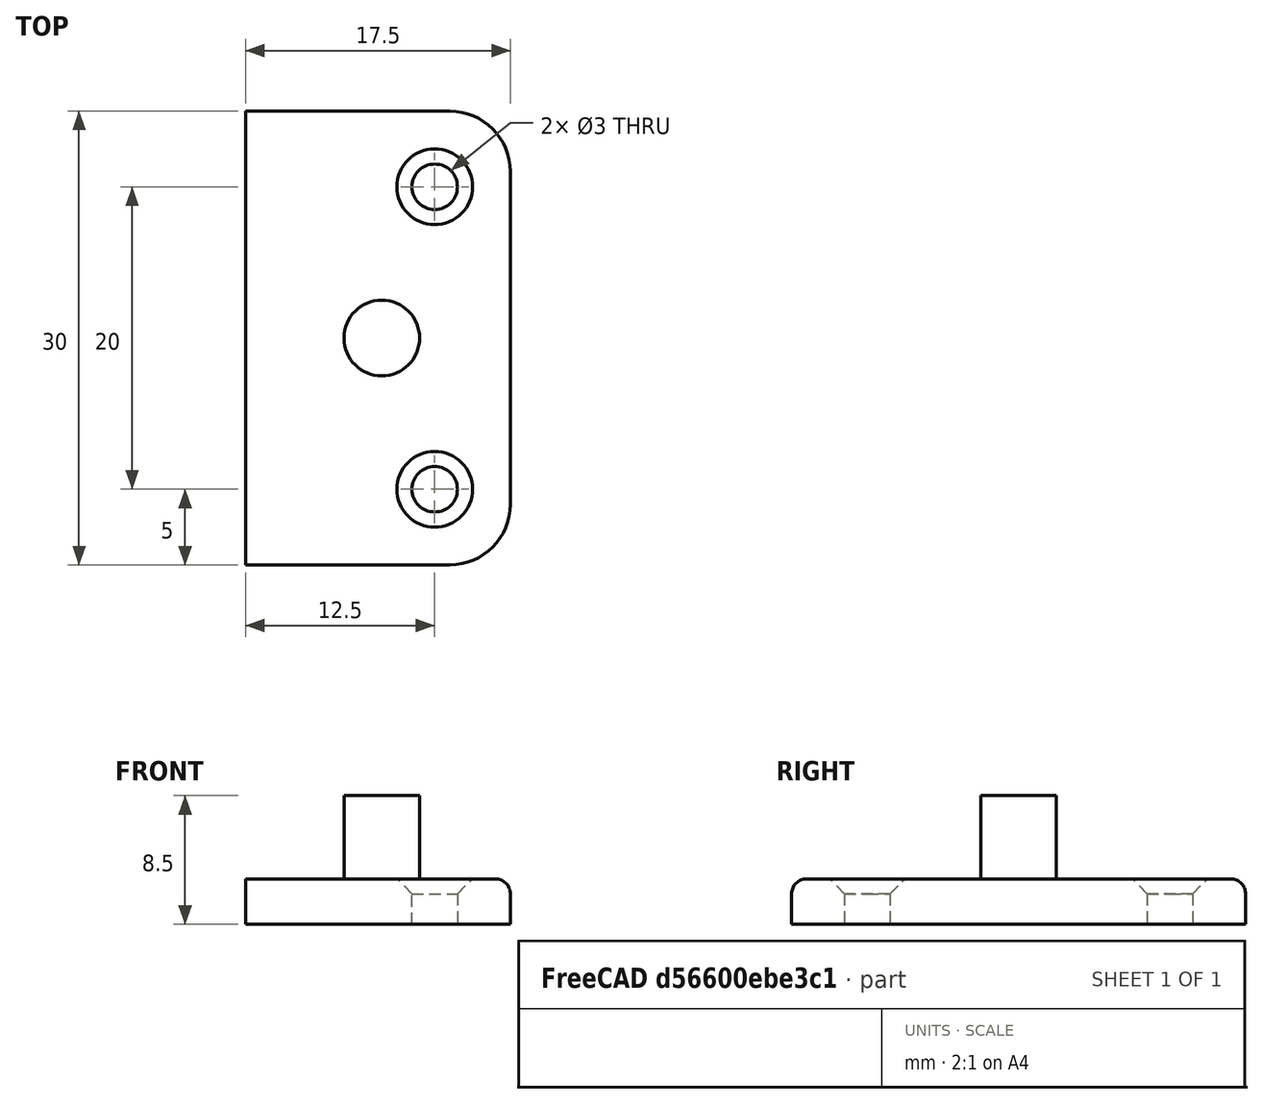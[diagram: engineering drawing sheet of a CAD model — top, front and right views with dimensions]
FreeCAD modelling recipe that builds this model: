
FCSTD DOCUMENT  (FreeCAD 0.20R29177 +426 (Git))
Label: project16
License: All rights reserved
LicenseURL: https://en.wikipedia.org/wiki/All_rights_reserved
objects: Sketcher::SketchObject×4, Part::Extrusion×2, Part::Fillet×2, PartDesign::Body×1, Part::Revolution×1, Part::Compound×1, Part::Chamfer×1, Part::Mirroring×1
note: 13 computed .brp shape members not serialized (recipe doc carries the construction recipe); baked Part::Feature solids carry a one-line shape summary decoded from their .brp

FEATURE [Sketcher::SketchObject] Sketch
  FullyConstrained = true
  MapMode = 5
  Placement = pos=(0,0,0) rot=(1,0,0;1.5708rad)
  Support = -> [XZ_Plane001]
  sketch-geometry (8):
    g0: GeomPoint X=0 Y=20 Z=0
    g1: GeomPoint X=4e-16 Y=15 Z=0
    g2: GeomPoint X=0 Y=3 Z=0
    g3: GeomPoint X=-17.5 Y=0 Z=0
    g4: GeomPoint X=-6.5 Y=0 Z=0
    g5: ArcOfCircle CenterX=0 CenterY=8.5 CenterZ=0 NormalX=0 NormalY=0 NormalZ=1 AngleXU=0 Radius=6.5 StartAngle=1.5708 EndAngle=3.14159
    g6: LineSegment StartX=-6.5 StartY=8.50001 StartZ=0 EndX=-6.5 EndY=3 EndZ=0
    g7: LineSegment StartX=-6.5 StartY=3 StartZ=0 EndX=-6.5 EndY=0 EndZ=0
  constraints (21):
    c: PointOnObject(g0,g-2)
    c: PointOnObject(g1,g-2)
    c: PointOnObject(g2,g-2)
    c: DistanceY(g-1,g0) = 20
    c: DistanceY(g1,g0) = 5
    c: DistanceY(g2,g1) = 12
    c: DistanceY(g-1,g2) = 3  'BaseHeight'
    c: PointOnObject(g3,g-1)
    c: DistanceX(g3,g-1) = 17.5  'BaseLength'
    c: PointOnObject(g4,g-1)
    c: DistanceX(g4,g-1) = 6.5
    c: Coincident(g5,g1)
    c: PointOnObject(g5,g-2)
    c: Diameter(g5) = 13
    c: Coincident(g6,g5)
    c: Coincident(g7,g4)
    c: Coincident(g6,g7)
    c: Vertical(g6)
    c: Vertical(g7)
    c: Horizontal(g6,g2)
    c: DistanceY(g6,g6) = 5.50001
FEATURE [Sketcher::SketchObject] Sketch001
  FullyConstrained = true
  MapMode = 5
  Support = -> [XY_Plane001]
  expr: Constraints[8] = Sketch.Constraints.BaseLength
  sketch-geometry (6):
    g0: LineSegment StartX=-17.5 StartY=15 StartZ=0 EndX=0 EndY=15 EndZ=0
    g1: LineSegment StartX=0 StartY=15 StartZ=0 EndX=0 EndY=-15 EndZ=0
    g2: LineSegment StartX=0 StartY=-15 StartZ=0 EndX=-17.5 EndY=-15 EndZ=0
    g3: LineSegment StartX=-17.5 StartY=-15 StartZ=0 EndX=-17.5 EndY=15 EndZ=0
    g4: Circle CenterX=-12.5 CenterY=10 CenterZ=0 NormalX=0 NormalY=0 NormalZ=1 AngleXU=0 Radius=1.5
    g5: Circle CenterX=-12.5 CenterY=-10 CenterZ=0 NormalX=0 NormalY=0 NormalZ=1 AngleXU=0 Radius=1.5
  constraints (17):
    c: Coincident(g0,g1)
    c: Coincident(g1,g2)
    c: Coincident(g2,g3)
    c: Coincident(g3,g0)
    c: Horizontal(g0)
    c: Horizontal(g2)
    c: Vertical(g3)
    c: PointOnObject(g1,g-2)
    c: DistanceX(g2,g2) = 17.5
    c: Symmetric(g0,g1,g-1)
    c: DistanceY(g3,g3) = 30
    c: Diameter(g4) = 3
    c: Equal(g5,g4)
    c: DistanceX(g0,g4) = 5
    c: DistanceY(g4,g0) = 5
    c: DistanceY(g2,g5) = 5
    c: DistanceX(g2,g5) = 5
FEATURE [Sketcher::SketchObject] Sketch002  label="Profile"
  AttachmentOffset = pos=(0,0,5.5) rot=(0,0,1;0rad)
  FullyConstrained = true
  MapMode = 5
  Placement = pos=(0,0,8.5) rot=(0,0,1;0rad)
  sketch-geometry (2):
    g0: Circle CenterX=-9 CenterY=0 CenterZ=0 NormalX=0 NormalY=0 NormalZ=1 AngleXU=0 Radius=2.5
    g1: GeomPoint X=-6.5 Y=0 Z=0
  constraints (5):
    c: PointOnObject(g0,g-1)
    c: Diameter(g0) = 5
    c: PointOnObject(g1,g0)
    c: PointOnObject(g1,g-1)
    c: DistanceX(g1,g-1) = 6.5
FEATURE [PartDesign::Body] Body001
  Group = -> [Sketch001,Sketch002,Sketch]
  Origin = -> Origin001
FEATURE [Part::Extrusion] Extrude
  Base = -> Sketch001
  Dir = (0,0,1)
  DirMode = 2
  FaceMakerClass = Part::FaceMakerBullseye
  LengthFwd = 3
  LengthRev = 0
  Solid = true
  Symmetric = false
FEATURE [Part::Extrusion] Extrude001
  Base = -> Sketch002
  Dir = (0,0,1)
  DirMode = 2
  FaceMakerClass = Part::FaceMakerBullseye
  LengthFwd = 5.5
  LengthRev = 0
  Reversed = true
  Solid = true
  Symmetric = false
FEATURE [Sketcher::SketchObject] Sketch003  label="Profile001"
  AttachmentOffset = pos=(0,0,5.5) rot=(0,0,1;0rad)
  FullyConstrained = true
  MapMode = 5
  Placement = pos=(0,0,8.5) rot=(0,0,1;0rad)
  sketch-geometry (2):
    g0: GeomPoint X=-6.5 Y=0 Z=0
    g1: LineSegment StartX=0 StartY=5 StartZ=0 EndX=0 EndY=-5 EndZ=0
  constraints (5):
    c: PointOnObject(g0,g-1)
    c: DistanceX(g0,g-1) = 6.5
    c: PointOnObject(g1,g-2)
    c: Symmetric(g1,g1,g-1)
    c: DistanceY(g1,g1) = 10
FEATURE [Part::Revolution] Revolve
  Angle = -90
  Axis = (0,-1,0)
  AxisLink = -> Sketch003 [Edge1]
  Base = (0,-5,8.5)
  FaceMakerClass = Part::FaceMakerBullseye
  Solid = false
  Source = -> Sketch002
  Symmetric = false
FEATURE [Part::Compound] Compound
  Links = -> [Extrude001,Extrude,Revolve]
FEATURE [Part::Chamfer] Chamfer
  Base = -> Compound
  Edges = 2 edges r=1: [Edge18,Edge21]
FEATURE [Part::Fillet] Fillet
  Base = -> Chamfer
  Edges = 2 edges r=4: [Edge16,Edge19]
FEATURE [Part::Fillet] Fillet001
  Base = -> Fillet
  Edges = 5 edges r=1: [Edge9,Edge13,Edge16,Edge18,Edge20]
FEATURE [Part::Mirroring] Part__Mirroring  label="Fillet001 (Mirror #1)"
  Base = (0,0,0)
  Normal = (1,0,0)
  Source = -> Fillet001
